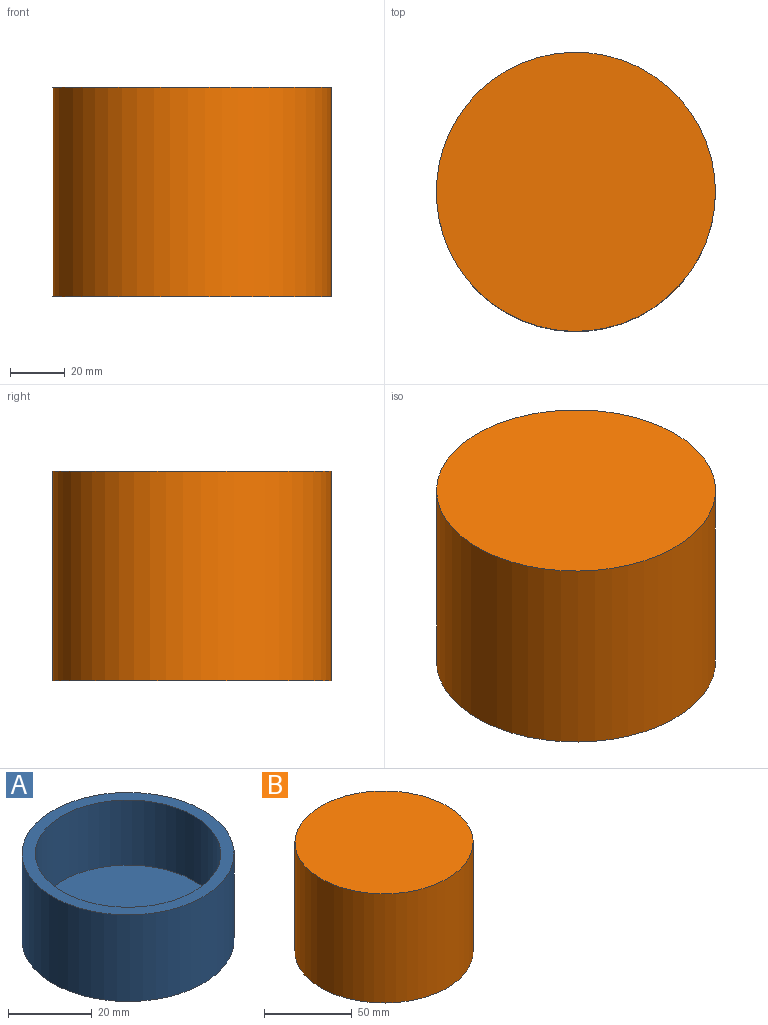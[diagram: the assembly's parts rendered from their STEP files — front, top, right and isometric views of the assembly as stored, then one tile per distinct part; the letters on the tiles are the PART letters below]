
ASSEMBLY  parts=2 mates=1
PART A: 5 faces, bbox 50.8x50.8x25.4 mm
  f0: cylinder r=22.23mm len=44.45mm, axis (0,0,-1), area 2660.2mm2, adj f2,f4
  f1: cylinder r=25.4mm len=50.8mm, axis (0,0,-1), area 4053.7mm2, adj f2,f3
  f2: plane 50.8x50.8mm, normal (0,0,1), area 475mm2, adj f0,f1
  f3: plane 50.8x50.8mm, normal (0,0,-1), area 2026.8mm2, adj f1
  f4: plane 44.45x44.45mm, normal (0,0,1), area 1551.8mm2, adj f0
PART B: 5 faces, bbox 101.6x101.6x76.2 mm
  f0: cylinder r=50.8mm len=101.6mm, axis (0,0,-1), area 24322mm2, adj f1,f2
  f1: plane 101.6x101.6mm, normal (0,0,1), area 8107.3mm2, adj f0
  f2: plane 101.6x101.6mm, normal (0,0,-1), area 981.7mm2, adj f0,f3
  f3: cylinder r=47.62mm len=95.25mm, axis (0,0,-1), area 20901.7mm2, adj f2,f4
  f4: plane 95.25x95.25mm, normal (0,0,-1), area 7125.6mm2, adj f3
PLACE A rot(axis=(-1,0,0),180deg) t=(-120.86,-72.05,24)mm
PLACE B t=(-57.29,-72.05,-45.85)mm
MATE slider A.f0 <-> B.f0  axis (0,0,1) through (-120.86,-72.05,24)mm
